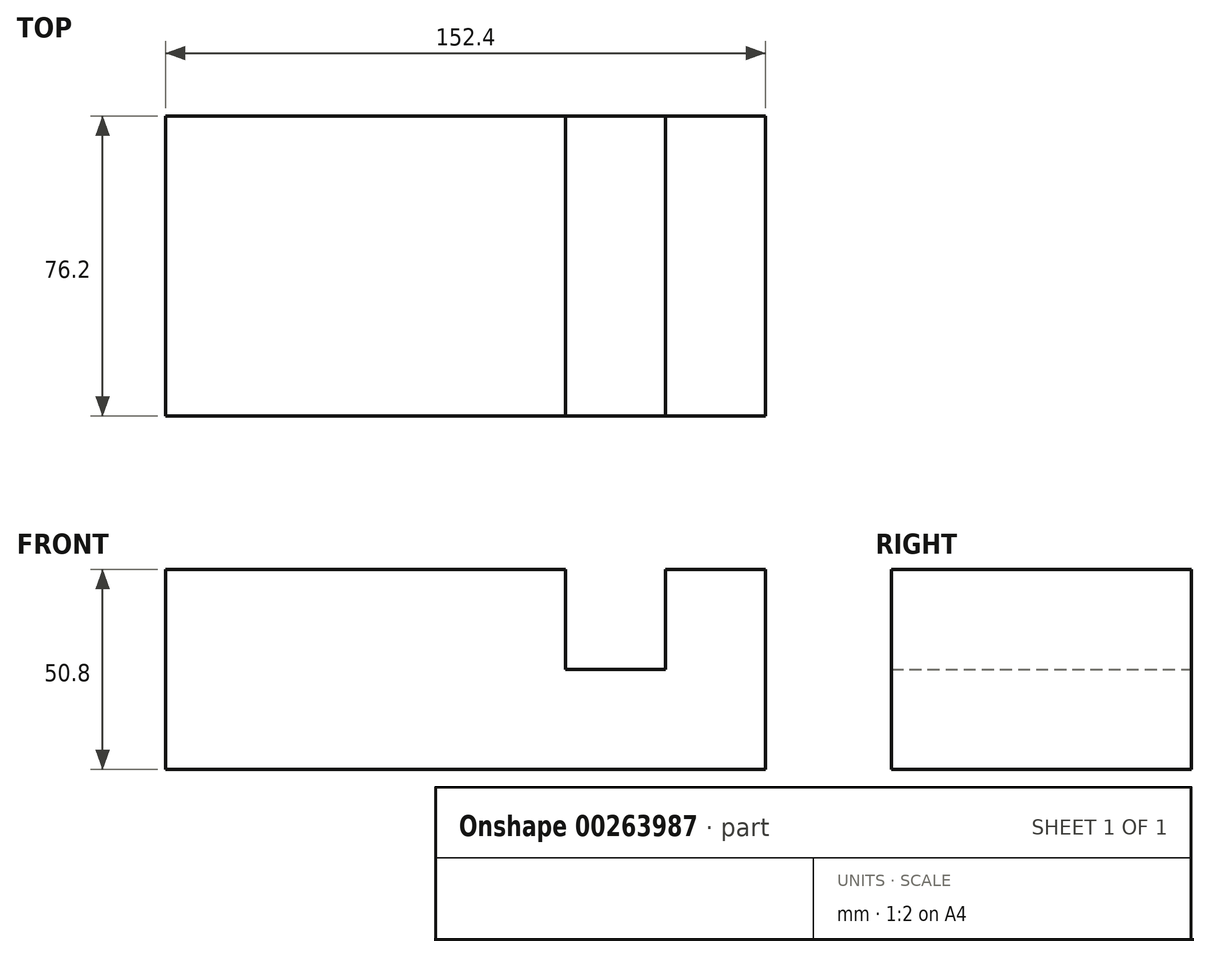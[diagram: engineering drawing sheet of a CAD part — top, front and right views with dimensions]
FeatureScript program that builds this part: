
annotation { "Feature Type Name" : "Feature", "Feature Type Description" : "" }
export const myFeature = defineFeature(function(context is Context, id is Id, definition is map)
    precondition{}
    {
        {
            var Q0;
            Q0=qCreatedBy(makeId("Front.planeOp"),FACE);
            var sketch = newSketch(context, id + "F0", { "sketchPlane" : qUnion([Q0])});
            skLineSegment(sketch, "E0", {"start": v(-75.98, 0) * mm, "end": v(76.42, 0) * mm});
            skLineSegment(sketch, "E1", {"start": v(76.42, 0) * mm, "end": v(76.42, 50.8) * mm});
            skLineSegment(sketch, "E2", {"start": v(76.42, 50.8) * mm, "end": v(51.02, 50.8) * mm});
            skLineSegment(sketch, "E3", {"start": v(51.02, 50.8) * mm, "end": v(51.02, 25.4) * mm});
            skLineSegment(sketch, "E4", {"start": v(51.02, 25.4) * mm, "end": v(25.62, 25.4) * mm});
            skLineSegment(sketch, "E5", {"start": v(25.62, 25.4) * mm, "end": v(25.62, 50.8) * mm});
            skLineSegment(sketch, "E6", {"start": v(25.62, 50.8) * mm, "end": v(-75.98, 50.8) * mm});
            skLineSegment(sketch, "E7", {"start": v(-75.98, 50.8) * mm, "end": v(-75.98, 0) * mm});
            skSolve(sketch);
        }
        {
            var Q0;
            Q0 = qSketchRegion(id + "F0", true);
            extrude(context, id + "F1", {"entities" : qUnion([Q0]), "depth" : 76.2 * mm});
        }
    });
